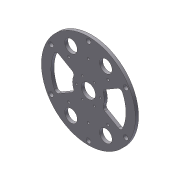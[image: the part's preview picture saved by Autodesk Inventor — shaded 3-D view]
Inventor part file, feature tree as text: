
AUTODESK INVENTOR PART (.ipt)
format: ipt  version: 2012 (Build 160160000, 160)  size: 192,000 bytes
history: native  units: in
note: dims shown in document units (in); Inventor stores cm internally (conversion verified against a paired STEP export)
features: extrude x6, sketch x6, pattern_circular x5
ambient origin geometry x8: Origin, YZ Plane, XZ Plane, XY Plane, X Axis, Y Axis, Z Axis, Center Point
bodies: Solid1 (feature_tree)
feature tree (17):
  extrude  "Extrusion1"  Depth=1.125in
  extrude  "Extrusion2"  Depth=1.875in
  pattern_circular  "Circular Pattern1"  Count=6 Angle=360.0deg
  extrude  "Extrusion5"  TaperAngle=0.0deg  [1 undecoded]
  pattern_circular  "Circular Pattern4"  Angle=45.0deg  [1 undecoded]
  extrude  "Extrusion6"  Depth=0.192in
  pattern_circular  "Circular Pattern5"  Count=2 Angle=360.0deg
  extrude  "Extrusion7"  Depth=6.8125in
  pattern_circular  "Circular Pattern6"  [2 undecoded]
  extrude  "Extrusion8"  Depth=1.0in TaperAngle=0.0deg
  pattern_circular  "Circular Pattern7"  Count=6 Angle=360.0deg
  sketch  "Sketch1"  dims[d0=7.425in d1=1.125in]
  sketch  "Sketch2"  dims[d2=0.25in d3=0.0in d4=1.875in]
  sketch  "Sketch6"  dims[d5=30.0deg]
  sketch  "Sketch7"  dims[d6=0.159in]
  sketch  "Sketch8"  dims[d7=0.25in d8=0.0in d9=2.3622in d10=360.0deg]
  sketch  "Sketch9"  dims[d32=4.375in d35=0.0in d36=0.0in d37=45.0deg d38=0.192in d39=0.7874in d40=360.0deg d42=6.8125in d43=0.375in d44=1.0in d45=0.0in d46=2.3622in d47=360.0deg d49=0.75in d50=1.25in d51=60.0deg d52=1.0in d53=0.0in d54=0.25in d55=0.7874in d56=360.0deg d59=1.0in d60=30.0deg d61=1.0in d62=0.0in d63=0.7874in d64=360.0deg d66=30.0deg d67=5.5in]
note: 4 required parameter values undecoded (feature->parameter linkage not recoverable at this tier; creation-order binding heuristic only, values carry confidence <= 0.55)
